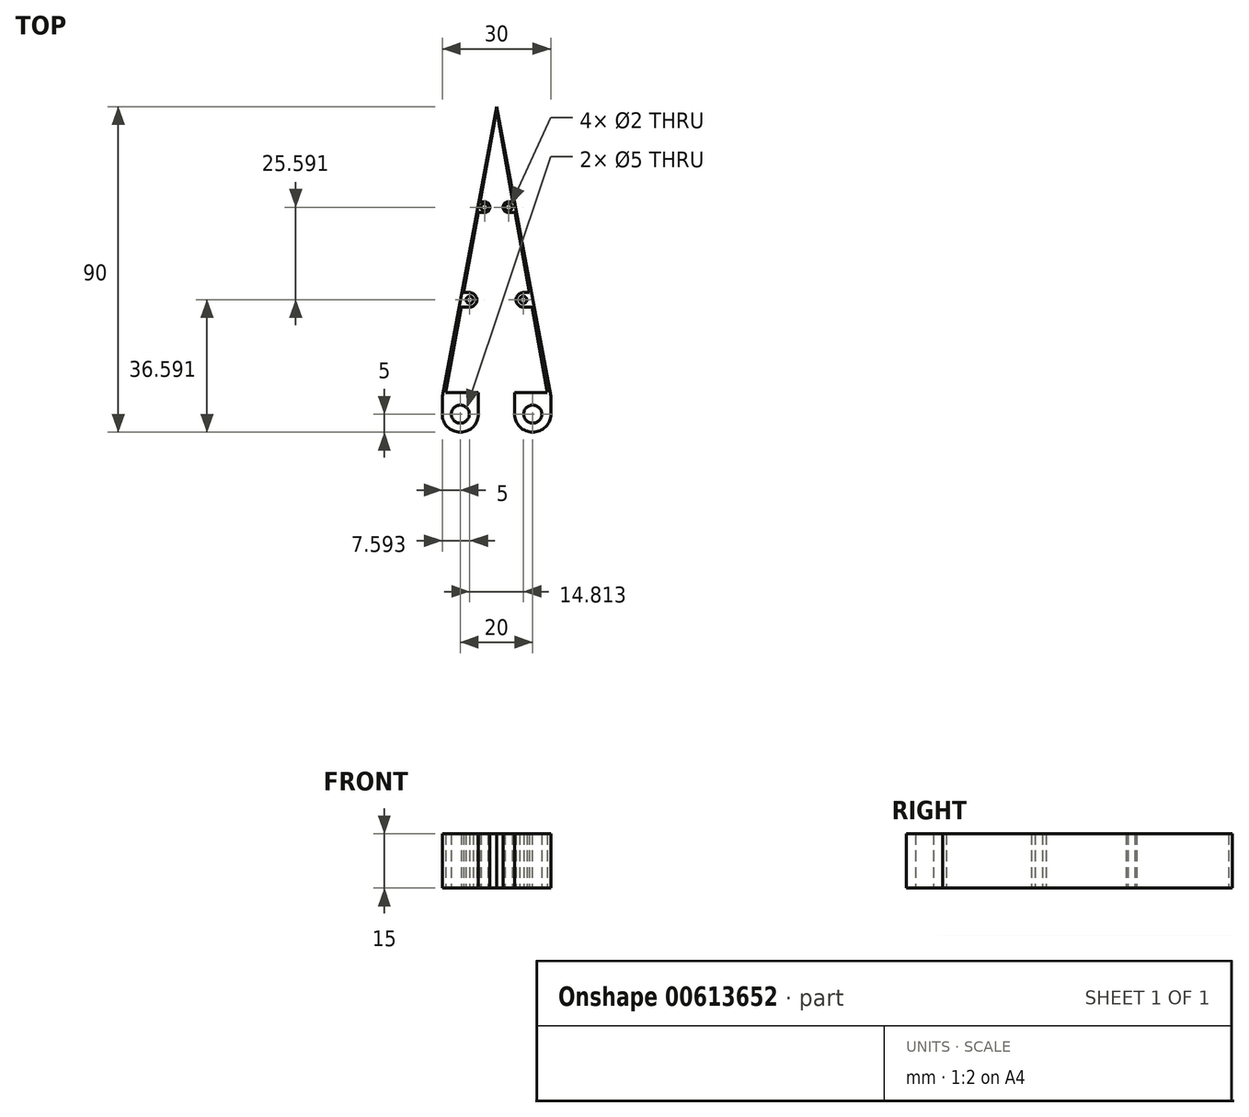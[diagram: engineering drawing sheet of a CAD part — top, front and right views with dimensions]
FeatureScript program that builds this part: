
annotation { "Feature Type Name" : "Feature", "Feature Type Description" : "" }
export const myFeature = defineFeature(function(context is Context, id is Id, definition is map)
    precondition{}
    {
        {
            var Q0;
            Q0=qCreatedBy(makeId("Top.planeOp"),FACE);
            var sketch = newSketch(context, id + "F0", { "sketchPlane" : qUnion([Q0])});
            skLineSegment(sketch, "E0", {"start": v(0, 0) * mm, "end": v(10, 0) * mm});
            skLineSegment(sketch, "E1", {"start": v(0, 0) * mm, "end": v(15, 80) * mm});
            skLineSegment(sketch, "E2", {"start": v(15, 80) * mm, "end": v(30, 0) * mm});
            skLineSegment(sketch, "E3", {"start": v(0, 0) * mm, "end": v(1, 0) * mm});
            skLineSegment(sketch, "E4", {"start": v(1, 1) * mm, "end": v(10, 1) * mm});
            skLineSegment(sketch, "E5", {"start": v(1, 1) * mm, "end": v(15, 79) * mm});
            skLineSegment(sketch, "E6", {"start": v(15, 79) * mm, "end": v(29, 1) * mm});
            skPoint(sketch, "E7.start.orphan", {"position": v(0, 80) * mm});
            skPoint(sketch, "E8.orphan", {"position": v(1, 79) * mm});
            skPoint(sketch, "E9.orphan", {"position": v(29, 79) * mm});
            skPoint(sketch, "E10.end.orphan", {"position": v(30, 80) * mm});
            skLineSegment(sketch, "E11", {"start": v(1, 1) * mm, "end": v(5.6, 26.6) * mm});
            skLineSegment(sketch, "E12", {"start": v(5.6, 26.6) * mm, "end": v(6.6, 26.6) * mm});
            skLineSegment(sketch, "E13", {"start": v(24.4, 26.6) * mm, "end": v(19.81, 52.18) * mm});
            skLineSegment(sketch, "E14", {"start": v(19.81, 52.18) * mm, "end": v(16.81, 52.18) * mm});
            skLineSegment(sketch, "E15", {"start": v(24.4, 26.6) * mm, "end": v(20.4, 26.6) * mm});
            skCircle(sketch, "E16", {"center": v(7.6, 26.6) * mm, "radius": 1 * mm});
            skArc(sketch, "E17", {"start": v(7.6, 24.6) * mm, "mid": v(9.6, 26.6) * mm, "end": v(7.6, 28.6) * mm});
            skCircle(sketch, "E18", {"center": v(22.4, 26.6) * mm, "radius": 1 * mm});
            skArc(sketch, "E19", {"start": v(22.4, 28.6) * mm, "mid": v(20.4, 26.6) * mm, "end": v(22.4, 24.6) * mm});
            skLineSegment(sketch, "E20", {"start": v(7.6, 26.6) * mm, "end": v(7.6, 28.6) * mm});
            skLineSegment(sketch, "E21", {"start": v(22.4, 28.6) * mm, "end": v(24.05, 28.6) * mm});
            skLineSegment(sketch, "E22", {"start": v(7.6, 28.6) * mm, "end": v(5.95, 28.6) * mm});
            skLineSegment(sketch, "E23", {"start": v(7.6, 26.6) * mm, "end": v(7.6, 24.6) * mm});
            skLineSegment(sketch, "E24", {"start": v(7.6, 24.6) * mm, "end": v(5.23, 24.6) * mm});
            skLineSegment(sketch, "E25", {"start": v(22.4, 24.6) * mm, "end": v(24.77, 24.6) * mm});
            skLineSegment(sketch, "E26.trimOffspring", {"start": v(20.4, 26.6) * mm, "end": v(24.4, 26.6) * mm});
            skLineSegment(sketch, "E27.trimOffspring", {"start": v(7.6, 26.6) * mm, "end": v(9.6, 26.6) * mm});
            skLineSegment(sketch, "E28", {"start": v(10.19, 52.18) * mm, "end": v(13.19, 52.18) * mm});
            skCircle(sketch, "E29", {"center": v(11.69, 52.18) * mm, "radius": 1 * mm});
            skCircle(sketch, "E30", {"center": v(18.31, 52.18) * mm, "radius": 1 * mm});
            skArc(sketch, "E31", {"start": v(18.31, 53.68) * mm, "mid": v(16.81, 52.18) * mm, "end": v(18.31, 50.68) * mm});
            skArc(sketch, "E32", {"start": v(11.69, 50.68) * mm, "mid": v(13.19, 52.18) * mm, "end": v(11.69, 53.68) * mm});
            skLineSegment(sketch, "E33", {"start": v(11.69, 52.18) * mm, "end": v(11.69, 53.68) * mm});
            skLineSegment(sketch, "E34", {"start": v(11.69, 53.68) * mm, "end": v(10.46, 53.68) * mm});
            skLineSegment(sketch, "E35", {"start": v(18.31, 53.68) * mm, "end": v(19.54, 53.68) * mm});
            skLineSegment(sketch, "E36", {"start": v(11.69, 52.18) * mm, "end": v(11.69, 50.68) * mm});
            skLineSegment(sketch, "E37", {"start": v(11.69, 50.68) * mm, "end": v(9.92, 50.68) * mm});
            skLineSegment(sketch, "E38", {"start": v(18.31, 50.68) * mm, "end": v(20.08, 50.68) * mm});
            skLineSegment(sketch, "E39.trimOffspring", {"start": v(13.19, 52.18) * mm, "end": v(10.19, 52.18) * mm});
            skLineSegment(sketch, "E40", {"start": v(30, 0) * mm, "end": v(20, 0) * mm});
            skLineSegment(sketch, "E41", {"start": v(5, -5) * mm, "end": v(5, -10) * mm});
            skArc(sketch, "E42", {"start": v(0, -5) * mm, "mid": v(5, -10) * mm, "end": v(10, -5) * mm});
            skLineSegment(sketch, "E43", {"start": v(5, -5) * mm, "end": v(10, -5) * mm});
            skLineSegment(sketch, "E44", {"start": v(10, -5) * mm, "end": v(10, 0) * mm});
            skLineSegment(sketch, "E45", {"start": v(5, -5) * mm, "end": v(0, -5) * mm});
            skLineSegment(sketch, "E46", {"start": v(0, -5) * mm, "end": v(0, 0) * mm});
            skCircle(sketch, "E47", {"center": v(5, -5) * mm, "radius": 2.5 * mm});
            skLineSegment(sketch, "E48", {"start": v(25, 0) * mm, "end": v(25, -10) * mm});
            skArc(sketch, "E49", {"start": v(20, -5) * mm, "mid": v(25, -10) * mm, "end": v(30, -5) * mm});
            skLineSegment(sketch, "E50", {"start": v(25, -5) * mm, "end": v(20, -5) * mm});
            skLineSegment(sketch, "E51", {"start": v(20, -5) * mm, "end": v(20, 0) * mm});
            skLineSegment(sketch, "E52", {"start": v(25, -5) * mm, "end": v(30, -5) * mm});
            skLineSegment(sketch, "E53", {"start": v(30, -5) * mm, "end": v(30, 0) * mm});
            skCircle(sketch, "E54", {"center": v(25, -5) * mm, "radius": 2.5 * mm});
            skLineSegment(sketch, "E55", {"start": v(10, 0) * mm, "end": v(10, 1) * mm});
            skLineSegment(sketch, "E56", {"start": v(20, 0) * mm, "end": v(20, 1) * mm});
            skLineSegment(sketch, "E57.trimOffspring", {"start": v(20, 0) * mm, "end": v(30, 0) * mm});
            skLineSegment(sketch, "E58.trimOffspring", {"start": v(20, 1) * mm, "end": v(29, 1) * mm});
            skSolve(sketch);
        }
        {
            var Q0;
            Q0 = qSketchRegion(id + "F0", true);
            var Q1;
            {var subQ1=sQuery(id+"F0.wireOp",EDGE,"E12");Q1=makeQuery(id+"F0.imprint","IMPRINT",FACE,{"disambiguationData":[TD([[makeQuery(id+"F0.imprint","IMPRINT",EDGE,{"derivedFrom":subQ1}),-1.0]])]});}
            var Q2;
            {var subQ0=sQuery(id+"F0.wireOp",EDGE,"E27.trimOffspring");var subQ1=sQuery(id+"F0.wireOp",EDGE,"E16");var subQ2=makeQuery(id+"F0.imprint","INTERSECT",VERTEX,{"derivedFrom":[subQ1,subQ0]});Q2=makeQuery(id+"F0.imprint","IMPRINT",FACE,{"disambiguationData":[TD([[makeQuery(id+"F0.imprint","IMPRINT",EDGE,{"disambiguationData":[TD([[subQ2,1.0]])],"derivedFrom":subQ1}),-1.0]])]});}
            var Q3;
            {var subQ0=sQuery(id+"F0.wireOp",EDGE,"E20");var subQ1=sQuery(id+"F0.wireOp",EDGE,"E16");var subQ2=makeQuery(id+"F0.imprint","INTERSECT",VERTEX,{"derivedFrom":[subQ1,subQ0]});Q3=makeQuery(id+"F0.imprint","IMPRINT",FACE,{"disambiguationData":[TD([[makeQuery(id+"F0.imprint","IMPRINT",EDGE,{"disambiguationData":[TD([[subQ2,1.0]])],"derivedFrom":subQ1}),-1.0]])]});}
            var Q4;
            {var subQ4=sQuery(id+"F0.wireOp",EDGE,"E12");Q4=makeQuery(id+"F0.imprint","IMPRINT",FACE,{"disambiguationData":[TD([[makeQuery(id+"F0.imprint","IMPRINT",EDGE,{"derivedFrom":subQ4}),1.0]])]});}
            var Q5;
            {var subQ0=sQuery(id+"F0.wireOp",EDGE,"E21");Q5=makeQuery(id+"F0.imprint","IMPRINT",FACE,{"disambiguationData":[TD([[makeQuery(id+"F0.imprint","IMPRINT",EDGE,{"derivedFrom":subQ0}),-1.0]])]});}
            var Q6;
            {var subQ0=sQuery(id+"F0.wireOp",EDGE,"E25");Q6=makeQuery(id+"F0.imprint","IMPRINT",FACE,{"disambiguationData":[TD([[makeQuery(id+"F0.imprint","IMPRINT",EDGE,{"derivedFrom":subQ0}),1.0]])]});}
            var Q7;
            {var subQ0=sQuery(id+"F0.wireOp",EDGE,"E37");Q7=makeQuery(id+"F0.imprint","IMPRINT",FACE,{"disambiguationData":[TD([[makeQuery(id+"F0.imprint","IMPRINT",EDGE,{"derivedFrom":subQ0}),-1.0]])]});}
            var Q8;
            {var subQ0=sQuery(id+"F0.wireOp",EDGE,"E39.trimOffspring");var subQ1=sQuery(id+"F0.wireOp",EDGE,"E29");var subQ2=makeQuery(id+"F0.imprint","INTERSECT",VERTEX,{"disambiguationData":[OD(0.0)],"derivedFrom":[subQ1,subQ0]});Q8=makeQuery(id+"F0.imprint","IMPRINT",FACE,{"disambiguationData":[TD([[makeQuery(id+"F0.imprint","IMPRINT",EDGE,{"disambiguationData":[TD([[subQ2,1.0]])],"derivedFrom":subQ1}),-1.0]])]});}
            var Q9;
            {var subQ0=sQuery(id+"F0.wireOp",EDGE,"E33");var subQ1=sQuery(id+"F0.wireOp",EDGE,"E29");var subQ2=makeQuery(id+"F0.imprint","INTERSECT",VERTEX,{"derivedFrom":[subQ1,subQ0]});Q9=makeQuery(id+"F0.imprint","IMPRINT",FACE,{"disambiguationData":[TD([[makeQuery(id+"F0.imprint","IMPRINT",EDGE,{"disambiguationData":[TD([[subQ2,1.0]])],"derivedFrom":subQ1}),-1.0]])]});}
            var Q10;
            {var subQ0=sQuery(id+"F0.wireOp",EDGE,"E34");Q10=makeQuery(id+"F0.imprint","IMPRINT",FACE,{"disambiguationData":[TD([[makeQuery(id+"F0.imprint","IMPRINT",EDGE,{"derivedFrom":subQ0}),1.0]])]});}
            var Q11;
            {var subQ8=sQuery(id+"F0.wireOp",EDGE,"E35");Q11=makeQuery(id+"F0.imprint","IMPRINT",FACE,{"disambiguationData":[TD([[makeQuery(id+"F0.imprint","IMPRINT",EDGE,{"derivedFrom":subQ8}),-1.0]])]});}
            var Q12;
            {var subQ8=sQuery(id+"F0.wireOp",EDGE,"E38");Q12=makeQuery(id+"F0.imprint","IMPRINT",FACE,{"disambiguationData":[TD([[makeQuery(id+"F0.imprint","IMPRINT",EDGE,{"derivedFrom":subQ8}),1.0]])]});}
            extrude(context, id + "F1", {"entities" : qUnion([Q0, Q1, Q2, Q3, Q4, Q5, Q6, Q7, Q8, Q9, Q10, Q11, Q12]), "depth" : 15 * mm, "offsetDistance" : 25 * mm});
        }
    });
